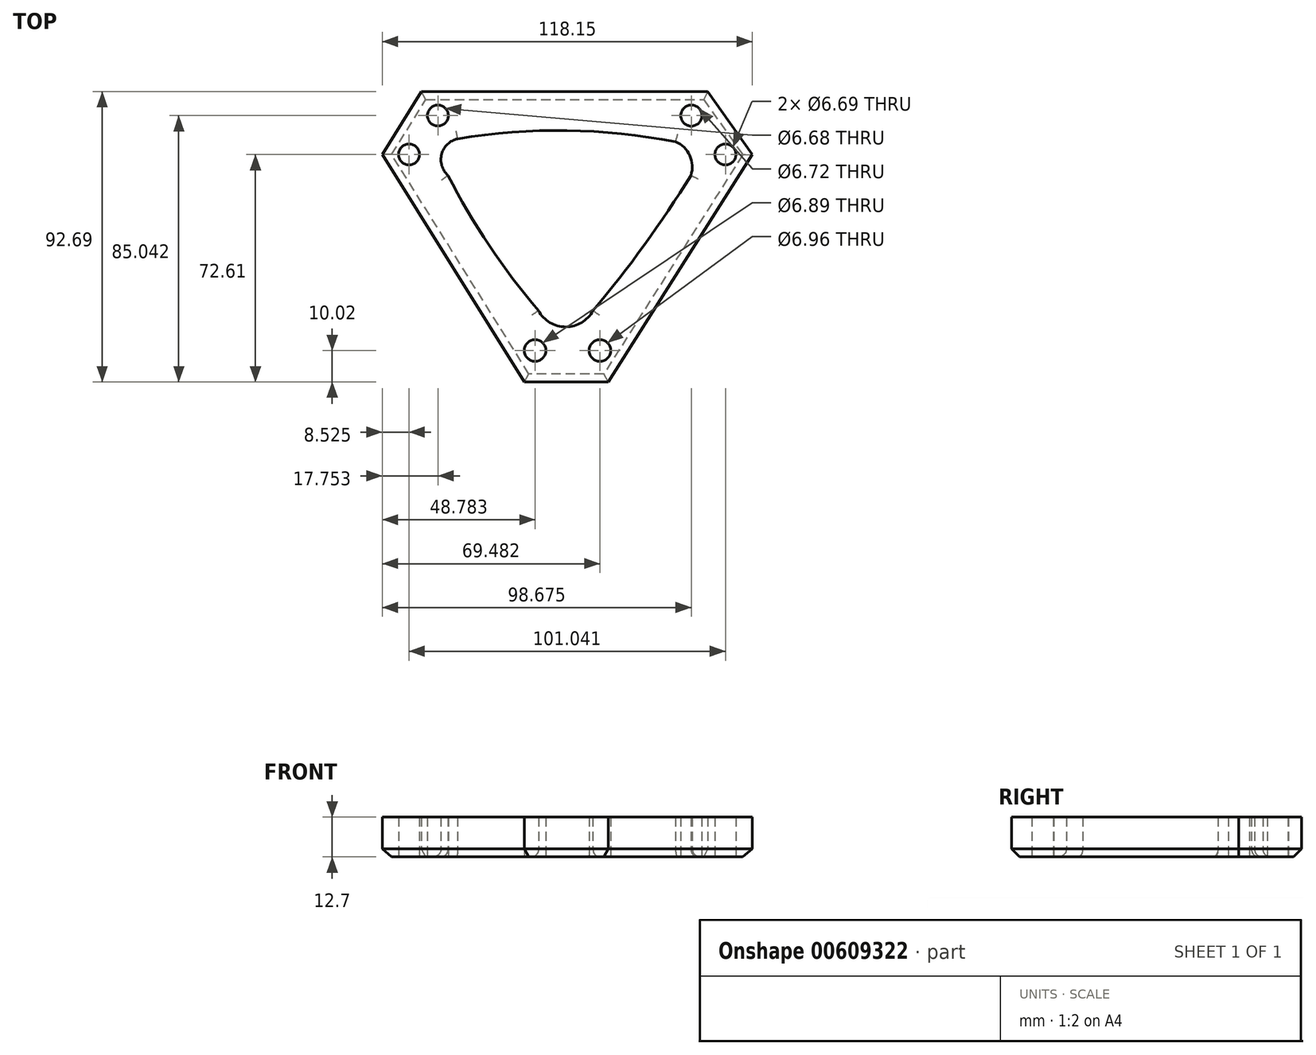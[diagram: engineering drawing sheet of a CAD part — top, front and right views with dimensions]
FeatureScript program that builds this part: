
annotation { "Feature Type Name" : "Feature", "Feature Type Description" : "" }
export const myFeature = defineFeature(function(context is Context, id is Id, definition is map)
    precondition{}
    {
        {
            var Q0;
            Q0=qCreatedBy(makeId("Top.planeOp"),FACE);
            var sketch = newSketch(context, id + "F0", { "sketchPlane" : qUnion([Q0])});
            skLineSegment(sketch, "E0", {"start": v(46.08, 45.94) * mm, "end": v(-45.32, 45.94) * mm});
            skLineSegment(sketch, "E1", {"start": v(46.08, 45.94) * mm, "end": v(60.32, 25.86) * mm});
            skLineSegment(sketch, "E2", {"start": v(-45.32, 45.94) * mm, "end": v(-57.83, 25.86) * mm});
            skLineSegment(sketch, "E3", {"start": v(60.32, 25.86) * mm, "end": v(14.3, -46.75) * mm});
            skLineSegment(sketch, "E4", {"start": v(-57.83, 25.86) * mm, "end": v(-12.44, -46.72) * mm});
            skLineSegment(sketch, "E5", {"start": v(14.3, -46.75) * mm, "end": v(-12.44, -46.72) * mm});
            skArc(sketch, "E6", {"start": v(35.8, 29.9) * mm, "mid": v(1.07, 33.5) * mm, "end": v(-33.75, 30.88) * mm});
            skArc(sketch, "E7", {"start": v(40.7, 19.2) * mm, "mid": v(40.36, 25.52) * mm, "end": v(35.8, 29.9) * mm});
            skArc(sketch, "E8", {"start": v(-33.75, 30.88) * mm, "mid": v(-38.88, 26) * mm, "end": v(-36.88, 19.2) * mm});
            skArc(sketch, "E9", {"start": v(9.43, -24) * mm, "mid": v(25.86, -2.98) * mm, "end": v(40.7, 19.2) * mm});
            skArc(sketch, "E10", {"start": v(-36.88, 19.2) * mm, "mid": v(-23.67, -3.23) * mm, "end": v(-7.96, -23.99) * mm});
            skArc(sketch, "E11", {"start": v(-7.96, -23.99) * mm, "mid": v(0.73, -29.19) * mm, "end": v(9.43, -24) * mm});
            skCircle(sketch, "E12", {"center": v(-40.08, 38.3) * mm, "radius": 3.34 * mm});
            skCircle(sketch, "E13", {"center": v(-49.3, 25.86) * mm, "radius": 3.34 * mm});
            skCircle(sketch, "E14", {"center": v(40.84, 38.3) * mm, "radius": 3.36 * mm});
            skCircle(sketch, "E15", {"center": v(51.74, 25.86) * mm, "radius": 3.34 * mm});
            skCircle(sketch, "E16", {"center": v(-9.05, -36.73) * mm, "radius": 3.44 * mm});
            skCircle(sketch, "E17", {"center": v(11.65, -36.73) * mm, "radius": 3.48 * mm});
            skSolve(sketch);
        }
        {
            var Q0;
            Q0=makeQuery(id+"F0.imprint","IMPRINT",FACE,{"disambiguationData":[TD([[makeQuery(id+"F0.imprint","IMPRINT",EDGE,{"derivedFrom":sQuery(id+"F0.wireOp",EDGE,"E0")}),1.0]])]});
            extrude(context, id + "F1", {"entities" : qUnion([Q0]), "depth" : 12.7 * mm, "offsetDistance" : 25.4 * mm});
        }
        {
            var Q0;
            Q0=makeQuery(id+"F1.opExtrude","CAP_EDGE",EDGE,{"disambiguationData":[OSD([sQuery(id+"F0.wireOp",EDGE,"E3")])],"isStart":true});
            var Q1;
            Q1=makeQuery(id+"F1.opExtrude","CAP_EDGE",EDGE,{"disambiguationData":[OSD([sQuery(id+"F0.wireOp",EDGE,"E5")])],"isStart":true});
            var Q2;
            Q2=makeQuery(id+"F1.opExtrude","CAP_EDGE",EDGE,{"disambiguationData":[OSD([sQuery(id+"F0.wireOp",EDGE,"E4")])],"isStart":true});
            var Q3;
            Q3=makeQuery(id+"F1.opExtrude","CAP_EDGE",EDGE,{"disambiguationData":[OSD([sQuery(id+"F0.wireOp",EDGE,"E2")])],"isStart":true});
            var Q4;
            Q4=makeQuery(id+"F1.opExtrude","CAP_EDGE",EDGE,{"disambiguationData":[OSD([sQuery(id+"F0.wireOp",EDGE,"E0")])],"isStart":true});
            var Q5;
            Q5=makeQuery(id+"F1.opExtrude","CAP_EDGE",EDGE,{"disambiguationData":[OSD([sQuery(id+"F0.wireOp",EDGE,"E1")])],"isStart":true});
            chamfer(context, id + "F2", {"entities" : qUnion([Q0, Q1, Q2, Q3, Q4, Q5]), "width" : 2.54 * mm, "tangentPropagation" : true});
        }
        {
            var Q0;
            Q0=makeQuery(id+"F1.opExtrude","CAP_EDGE",EDGE,{"disambiguationData":[OSD([sQuery(id+"F0.wireOp",EDGE,"E9")])],"isStart":true});
            var Q1;
            Q1=makeQuery(id+"F1.opExtrude","CAP_EDGE",EDGE,{"disambiguationData":[OSD([sQuery(id+"F0.wireOp",EDGE,"E7")])],"isStart":true});
            var Q2;
            Q2=makeQuery(id+"F1.opExtrude","CAP_EDGE",EDGE,{"disambiguationData":[OSD([sQuery(id+"F0.wireOp",EDGE,"E6")])],"isStart":true});
            var Q3;
            Q3=makeQuery(id+"F1.opExtrude","CAP_EDGE",EDGE,{"disambiguationData":[OSD([sQuery(id+"F0.wireOp",EDGE,"E10")])],"isStart":true});
            var Q4;
            Q4=makeQuery(id+"F1.opExtrude","CAP_EDGE",EDGE,{"disambiguationData":[OSD([sQuery(id+"F0.wireOp",EDGE,"E11")])],"isStart":true});
            fillet(context, id + "F3", {"entities" : qUnion([Q0, Q1, Q2, Q3, Q4]), "radius" : 2.54 * mm, "tangentPropagation" : true, "allowEdgeOverflow" : false});
        }
        {
            var Q0;
            Q0=makeQuery(id+"F1.opExtrude","CAP_EDGE",EDGE,{"disambiguationData":[OSD([sQuery(id+"F0.wireOp",EDGE,"E12")])],"isStart":true});
            var Q1;
            Q1=makeQuery(id+"F1.opExtrude","CAP_EDGE",EDGE,{"disambiguationData":[OSD([sQuery(id+"F0.wireOp",EDGE,"E13")])],"isStart":true});
            var Q2;
            Q2=makeQuery(id+"F1.opExtrude","CAP_EDGE",EDGE,{"disambiguationData":[OSD([sQuery(id+"F0.wireOp",EDGE,"E16")])],"isStart":true});
            var Q3;
            Q3=makeQuery(id+"F1.opExtrude","CAP_EDGE",EDGE,{"disambiguationData":[OSD([sQuery(id+"F0.wireOp",EDGE,"E15")])],"isStart":true});
            var Q4;
            Q4=makeQuery(id+"F1.opExtrude","CAP_EDGE",EDGE,{"disambiguationData":[OSD([sQuery(id+"F0.wireOp",EDGE,"E14")])],"isStart":true});
            var Q5;
            Q5=makeQuery(id+"F1.opExtrude","CAP_EDGE",EDGE,{"disambiguationData":[OSD([sQuery(id+"F0.wireOp",EDGE,"E17")])],"isStart":true});
            fillet(context, id + "F4", {"entities" : qUnion([Q0, Q1, Q2, Q3, Q4, Q5]), "radius" : 0.25 * mm, "tangentPropagation" : true, "allowEdgeOverflow" : false});
        }
    });
